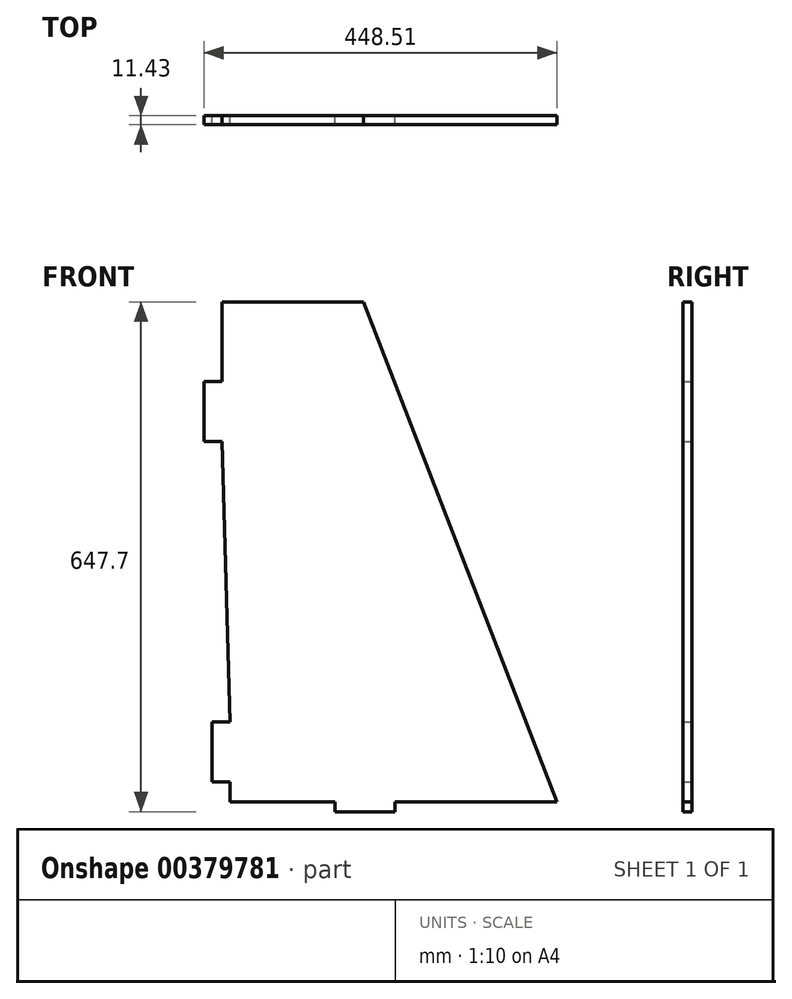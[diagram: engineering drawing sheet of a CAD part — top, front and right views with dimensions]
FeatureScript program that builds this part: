
annotation { "Feature Type Name" : "Feature", "Feature Type Description" : "" }
export const myFeature = defineFeature(function(context is Context, id is Id, definition is map)
    precondition{}
    {
        {
            var Q0;
            Q0=qCreatedBy(makeId("Front.planeOp"),FACE);
            var sketch = newSketch(context, id + "F0", { "sketchPlane" : qUnion([Q0])});
            skLineSegment(sketch, "E0", {"start": v(-143.4, 458.4) * mm, "end": v(36.12, 458.4) * mm});
            skLineSegment(sketch, "E1", {"start": v(36.12, 458.4) * mm, "end": v(282.25, -176.6) * mm});
            skLineSegment(sketch, "E2", {"start": v(0, -202) * mm, "end": v(76.2, -202) * mm});
            skLineSegment(sketch, "E3", {"start": v(-143.4, 357.38) * mm, "end": v(-166.26, 357.38) * mm});
            skLineSegment(sketch, "E4", {"start": v(-166.26, 357.38) * mm, "end": v(-166.26, 281.18) * mm});
            skLineSegment(sketch, "E5", {"start": v(-166.26, 281.18) * mm, "end": v(-143.4, 281.18) * mm});
            skLineSegment(sketch, "E6", {"start": v(-133.24, -151.2) * mm, "end": v(-156.1, -151.2) * mm});
            skLineSegment(sketch, "E7", {"start": v(-156.1, -151.2) * mm, "end": v(-156.1, -75) * mm});
            skLineSegment(sketch, "E8", {"start": v(-156.1, -75) * mm, "end": v(-133.24, -75) * mm});
            skLineSegment(sketch, "E9", {"start": v(0, -176.6) * mm, "end": v(-133.24, -176.6) * mm});
            skLineSegment(sketch, "E10", {"start": v(76.2, -176.6) * mm, "end": v(282.25, -176.6) * mm});
            skLineSegment(sketch, "E11", {"start": v(-133.24, -151.2) * mm, "end": v(-133.24, -176.6) * mm});
            skLineSegment(sketch, "E12", {"start": v(-143.4, 357.38) * mm, "end": v(-143.4, 458.4) * mm});
            skLineSegment(sketch, "E13", {"start": v(-143.4, 281.18) * mm, "end": v(-133.24, -75) * mm});
            skLineSegment(sketch, "E14", {"start": v(0, -176.6) * mm, "end": v(0, -189.3) * mm});
            skLineSegment(sketch, "E15", {"start": v(76.2, -176.6) * mm, "end": v(76.2, -189.3) * mm});
            skLineSegment(sketch, "E16", {"start": v(0, -189.3) * mm, "end": v(76.2, -189.3) * mm});
            skSolve(sketch);
        }
        {
            var Q0;
            Q0=makeQuery(id+"F0.imprint","IMPRINT",FACE,{"disambiguationData":[TD([[makeQuery(id+"F0.imprint","IMPRINT",EDGE,{"derivedFrom":sQuery(id+"F0.wireOp",EDGE,"E0")}),-1.0]])]});
            extrude(context, id + "F1", {"entities" : qUnion([Q0]), "depth" : 11.43 * mm});
        }
    });
